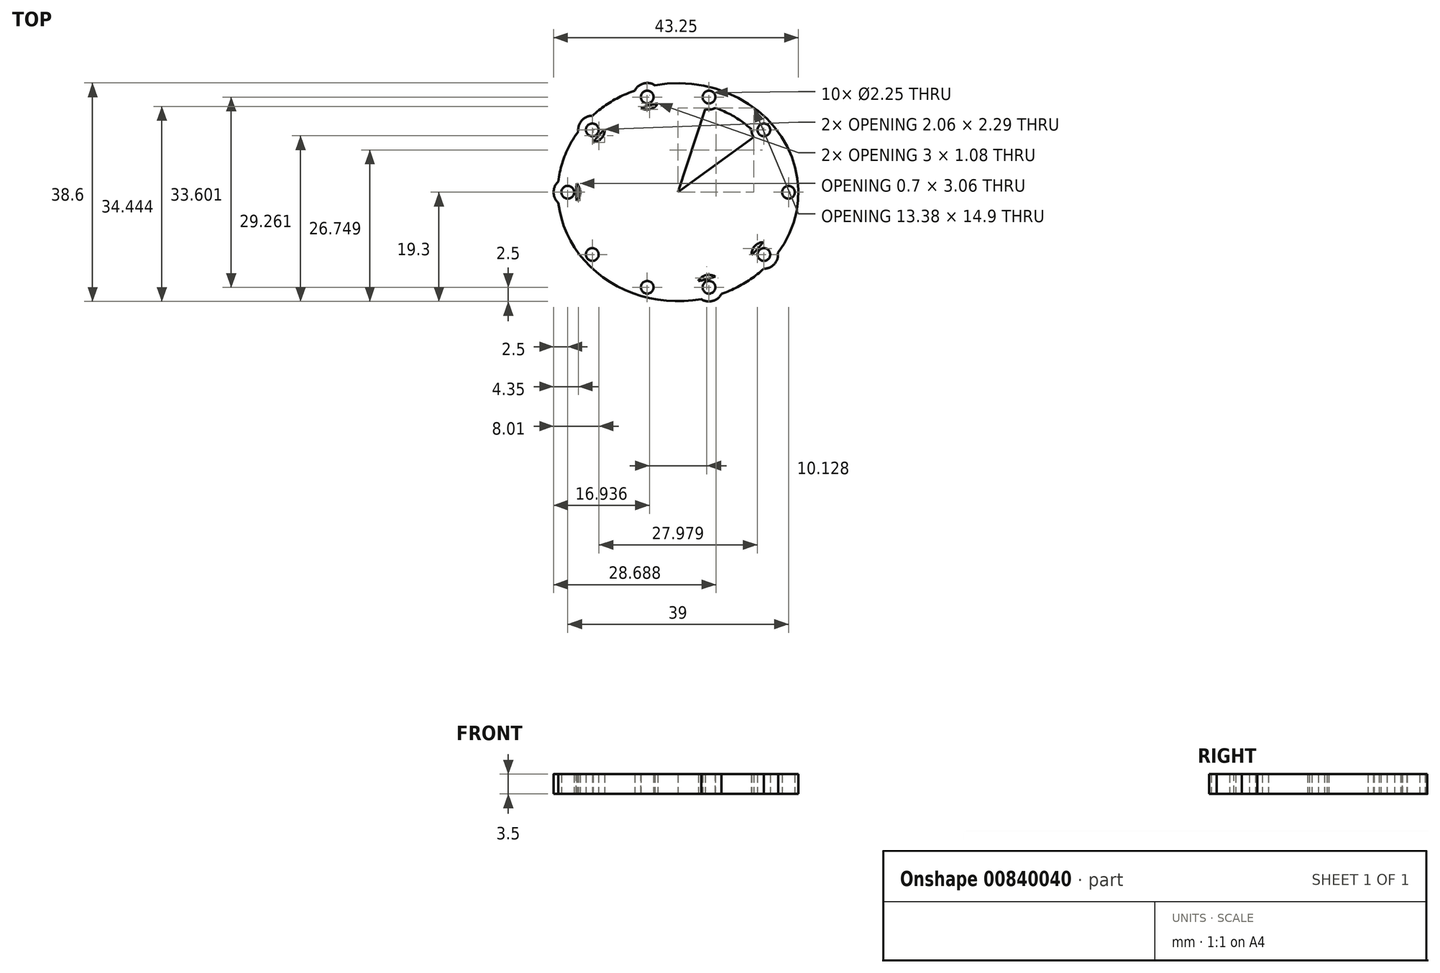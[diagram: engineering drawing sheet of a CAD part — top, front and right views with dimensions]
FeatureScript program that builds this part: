
annotation { "Feature Type Name" : "Feature", "Feature Type Description" : "" }
export const myFeature = defineFeature(function(context is Context, id is Id, definition is map)
    precondition{}
    {
        {
            var Q0;
            Q0=qCreatedBy(makeId("Top.planeOp"),FACE);
            var sketch = newSketch(context, id + "F0", { "sketchPlane" : qUnion([Q0])});
            skEllipse(sketch, "E0", {"center": v(0, 0) * mm, "majorRadius": 18 * mm, "minorRadius": 16 * mm, "majorAxis": v(1, 0)});
            skEllipse(sketch, "E1", {"center": v(0, 0) * mm, "majorRadius": 19.5 * mm, "minorRadius": 17.5 * mm, "majorAxis": v(1, 0)});
            skEllipse(sketch, "E2", {"center": v(0, 0) * mm, "majorRadius": 21.25 * mm, "minorRadius": 19.25 * mm, "majorAxis": v(1, 0)});
            skLineSegment(sketch, "E3", {"start": v(0, 0) * mm, "end": v(8.4, 25.87) * mm});
            skCircle(sketch, "E4", {"center": v(5.46, 16.8) * mm, "radius": 1.13 * mm});
            skLineSegment(sketch, "E5", {"start": v(0, 0) * mm, "end": v(30, 21.8) * mm});
            skCircle(sketch, "E6", {"center": v(15.16, 11.01) * mm, "radius": 1.13 * mm});
            skCircle(sketch, "E7", {"center": v(19.5, 0) * mm, "radius": 1.13 * mm});
            skCircle(sketch, "E8.MirrorC", {"center": v(15.16, -11.01) * mm, "radius": 1.13 * mm});
            skCircle(sketch, "E9.MirrorC", {"center": v(5.46, -16.8) * mm, "radius": 1.13 * mm});
            skCircle(sketch, "E10.MirrorC", {"center": v(-5.46, -16.8) * mm, "radius": 1.13 * mm});
            skCircle(sketch, "E11.MirrorC", {"center": v(-15.16, -11.01) * mm, "radius": 1.13 * mm});
            skCircle(sketch, "E12.MirrorC", {"center": v(-19.5, 0) * mm, "radius": 1.13 * mm});
            skCircle(sketch, "E13.MirrorC", {"center": v(-15.16, 11.01) * mm, "radius": 1.13 * mm});
            skCircle(sketch, "E14.MirrorC", {"center": v(-5.46, 16.8) * mm, "radius": 1.13 * mm});
            skArc(sketch, "E15", {"start": v(3.56, 15.68) * mm, "mid": v(4.9, 14.67) * mm, "end": v(6.56, 14.9) * mm});
            skArc(sketch, "E16", {"start": v(4.09, 18.9) * mm, "mid": v(6.1, 19.22) * mm, "end": v(7.68, 17.95) * mm});
            skArc(sketch, "E17", {"start": v(15.14, 13.51) * mm, "mid": v(17.01, 12.69) * mm, "end": v(17.64, 10.73) * mm});
            skArc(sketch, "E18", {"start": v(12.96, 11.1) * mm, "mid": v(13.52, 9.54) * mm, "end": v(15.02, 8.82) * mm});
            skArc(sketch, "E19", {"start": v(21.15, 1.88) * mm, "mid": v(22, 0) * mm, "end": v(21.15, -1.88) * mm});
            skArc(sketch, "E20", {"start": v(17.92, 1.53) * mm, "mid": v(17.3, 0) * mm, "end": v(17.92, -1.53) * mm});
            skArc(sketch, "E21.MirrorCS", {"start": v(12.96, -11.1) * mm, "mid": v(13.52, -9.54) * mm, "end": v(15.02, -8.82) * mm});
            skArc(sketch, "E22.MirrorCS", {"start": v(15.14, -13.51) * mm, "mid": v(17.01, -12.69) * mm, "end": v(17.64, -10.73) * mm});
            skArc(sketch, "E23.MirrorCS", {"start": v(3.56, -15.68) * mm, "mid": v(4.9, -14.67) * mm, "end": v(6.56, -14.9) * mm});
            skArc(sketch, "E24.MirrorCS", {"start": v(4.09, -18.9) * mm, "mid": v(6.1, -19.22) * mm, "end": v(7.68, -17.95) * mm});
            skArc(sketch, "E25.MirrorCS", {"start": v(-4.09, -18.9) * mm, "mid": v(-6.1, -19.22) * mm, "end": v(-7.68, -17.95) * mm});
            skArc(sketch, "E26.MirrorCS", {"start": v(-3.56, -15.68) * mm, "mid": v(-4.9, -14.67) * mm, "end": v(-6.56, -14.9) * mm});
            skArc(sketch, "E27.MirrorCS", {"start": v(-15.14, -13.51) * mm, "mid": v(-17.01, -12.69) * mm, "end": v(-17.64, -10.73) * mm});
            skArc(sketch, "E28.MirrorCS", {"start": v(-12.96, -11.1) * mm, "mid": v(-13.52, -9.54) * mm, "end": v(-15.02, -8.82) * mm});
            skArc(sketch, "E29.MirrorCS", {"start": v(-17.92, 1.53) * mm, "mid": v(-17.3, 0) * mm, "end": v(-17.92, -1.53) * mm});
            skArc(sketch, "E30.MirrorCS", {"start": v(-21.15, 1.88) * mm, "mid": v(-22, 0) * mm, "end": v(-21.15, -1.88) * mm});
            skArc(sketch, "E31.MirrorCS", {"start": v(-12.96, 11.1) * mm, "mid": v(-13.52, 9.54) * mm, "end": v(-15.02, 8.82) * mm});
            skArc(sketch, "E32.MirrorCS", {"start": v(-15.14, 13.51) * mm, "mid": v(-17.01, 12.69) * mm, "end": v(-17.64, 10.73) * mm});
            skArc(sketch, "E33.MirrorCS", {"start": v(-3.56, 15.68) * mm, "mid": v(-4.9, 14.67) * mm, "end": v(-6.56, 14.9) * mm});
            skArc(sketch, "E34.MirrorCS", {"start": v(-4.09, 18.9) * mm, "mid": v(-6.1, 19.22) * mm, "end": v(-7.68, 17.95) * mm});
            skSolve(sketch);
        }
        {
            var Q0;
            {var subQ9=sQuery(id+"F0.wireOp",EDGE,"E1");var subQ36=sQuery(id+"F0.wireOp",EDGE,"E6");var subQ37=makeQuery(id+"F0.imprint","INTERSECT",VERTEX,{"disambiguationData":[OD(0.0)],"derivedFrom":[subQ9,subQ36]});Q0=makeQuery(id+"F0.imprint","IMPRINT",FACE,{"disambiguationData":[TD([[makeQuery(id+"F0.imprint","IMPRINT",EDGE,{"disambiguationData":[TD([[subQ37,1.0]])],"derivedFrom":subQ9}),-1.0]])]});}
            var Q1;
            {var subQ6=sQuery(id+"F0.wireOp",EDGE,"E0");var subQ31=makeQuery(id+"F0.imprint","INTERSECT",VERTEX,{"disambiguationData":[OD(1.0)],"derivedFrom":[subQ6,sQuery(id+"F0.wireOp",EDGE,"E18")]});Q1=makeQuery(id+"F0.imprint","IMPRINT",FACE,{"disambiguationData":[TD([[makeQuery(id+"F0.imprint","IMPRINT",EDGE,{"disambiguationData":[TD([[subQ31,1.0]])],"derivedFrom":subQ6}),-1.0]])]});}
            var Q2;
            {var subQ5=sQuery(id+"F0.wireOp",EDGE,"E6");var subQ6=sQuery(id+"F0.wireOp",EDGE,"E1");var subQ7=makeQuery(id+"F0.imprint","INTERSECT",VERTEX,{"disambiguationData":[OD(1.0)],"derivedFrom":[subQ6,subQ5]});Q2=makeQuery(id+"F0.imprint","IMPRINT",FACE,{"disambiguationData":[TD([[makeQuery(id+"F0.imprint","IMPRINT",EDGE,{"disambiguationData":[TD([[subQ7,-1.0]])],"derivedFrom":subQ6}),-1.0]])]});}
            var Q3;
            {var subQ5=sQuery(id+"F0.wireOp",EDGE,"E0");var subQ7=makeQuery(id+"F0.imprint","INTERSECT",VERTEX,{"disambiguationData":[OD(0.0)],"derivedFrom":[subQ5,sQuery(id+"F0.wireOp",EDGE,"E18")]});Q3=makeQuery(id+"F0.imprint","IMPRINT",FACE,{"disambiguationData":[TD([[makeQuery(id+"F0.imprint","IMPRINT",EDGE,{"disambiguationData":[TD([[subQ7,1.0]])],"derivedFrom":subQ5}),-1.0]])]});}
            var Q4;
            {var subQ0=sQuery(id+"F0.wireOp",EDGE,"E16");var subQ1=sQuery(id+"F0.wireOp",EDGE,"E2");var subQ2=makeQuery(id+"F0.imprint","INTERSECT",VERTEX,{"disambiguationData":[OD(1.0)],"derivedFrom":[subQ1,subQ0]});Q4=makeQuery(id+"F0.imprint","IMPRINT",FACE,{"disambiguationData":[TD([[makeQuery(id+"F0.imprint","IMPRINT",EDGE,{"disambiguationData":[TD([[subQ2,-1.0]])],"derivedFrom":subQ1}),-1.0]])]});}
            var Q5;
            {var subQ0=sQuery(id+"F0.wireOp",EDGE,"E16");var subQ1=sQuery(id+"F0.wireOp",EDGE,"E2");var subQ2=makeQuery(id+"F0.imprint","INTERSECT",VERTEX,{"disambiguationData":[OD(0.0)],"derivedFrom":[subQ1,subQ0]});Q5=makeQuery(id+"F0.imprint","IMPRINT",FACE,{"disambiguationData":[TD([[makeQuery(id+"F0.imprint","IMPRINT",EDGE,{"disambiguationData":[TD([[subQ2,1.0]])],"derivedFrom":subQ1}),-1.0]])]});}
            var Q6;
            {var subQ0=sQuery(id+"F0.wireOp",EDGE,"E15");var subQ1=sQuery(id+"F0.wireOp",EDGE,"E0");var subQ2=makeQuery(id+"F0.imprint","INTERSECT",VERTEX,{"disambiguationData":[OD(0.0)],"derivedFrom":[subQ1,subQ0]});Q6=makeQuery(id+"F0.imprint","IMPRINT",FACE,{"disambiguationData":[TD([[makeQuery(id+"F0.imprint","IMPRINT",EDGE,{"disambiguationData":[TD([[subQ2,1.0]])],"derivedFrom":subQ1}),1.0]])]});}
            var Q7;
            {var subQ0=sQuery(id+"F0.wireOp",EDGE,"E15");var subQ1=sQuery(id+"F0.wireOp",EDGE,"E0");var subQ2=makeQuery(id+"F0.imprint","INTERSECT",VERTEX,{"disambiguationData":[OD(1.0)],"derivedFrom":[subQ1,subQ0]});Q7=makeQuery(id+"F0.imprint","IMPRINT",FACE,{"disambiguationData":[TD([[makeQuery(id+"F0.imprint","IMPRINT",EDGE,{"disambiguationData":[TD([[subQ2,-1.0]])],"derivedFrom":subQ1}),1.0]])]});}
            var Q8;
            {var subQ0=sQuery(id+"F0.wireOp",EDGE,"E17");var subQ1=sQuery(id+"F0.wireOp",EDGE,"E2");var subQ2=makeQuery(id+"F0.imprint","INTERSECT",VERTEX,{"disambiguationData":[OD(0.0)],"derivedFrom":[subQ1,subQ0]});Q8=makeQuery(id+"F0.imprint","IMPRINT",FACE,{"disambiguationData":[TD([[makeQuery(id+"F0.imprint","IMPRINT",EDGE,{"disambiguationData":[TD([[subQ2,1.0]])],"derivedFrom":subQ1}),-1.0]])]});}
            var Q9;
            {var subQ0=sQuery(id+"F0.wireOp",EDGE,"E17");var subQ1=sQuery(id+"F0.wireOp",EDGE,"E2");var subQ2=makeQuery(id+"F0.imprint","INTERSECT",VERTEX,{"disambiguationData":[OD(1.0)],"derivedFrom":[subQ1,subQ0]});Q9=makeQuery(id+"F0.imprint","IMPRINT",FACE,{"disambiguationData":[TD([[makeQuery(id+"F0.imprint","IMPRINT",EDGE,{"disambiguationData":[TD([[subQ2,-1.0]])],"derivedFrom":subQ1}),-1.0]])]});}
            var Q10;
            {var subQ0=sQuery(id+"F0.wireOp",EDGE,"E18");var subQ1=sQuery(id+"F0.wireOp",EDGE,"E0");var subQ2=makeQuery(id+"F0.imprint","INTERSECT",VERTEX,{"disambiguationData":[OD(1.0)],"derivedFrom":[subQ1,subQ0]});Q10=makeQuery(id+"F0.imprint","IMPRINT",FACE,{"disambiguationData":[TD([[makeQuery(id+"F0.imprint","IMPRINT",EDGE,{"disambiguationData":[TD([[subQ2,-1.0]])],"derivedFrom":subQ1}),1.0]])]});}
            var Q11;
            {var subQ0=sQuery(id+"F0.wireOp",EDGE,"E18");var subQ1=sQuery(id+"F0.wireOp",EDGE,"E0");var subQ2=makeQuery(id+"F0.imprint","INTERSECT",VERTEX,{"disambiguationData":[OD(0.0)],"derivedFrom":[subQ1,subQ0]});Q11=makeQuery(id+"F0.imprint","IMPRINT",FACE,{"disambiguationData":[TD([[makeQuery(id+"F0.imprint","IMPRINT",EDGE,{"disambiguationData":[TD([[subQ2,1.0]])],"derivedFrom":subQ1}),1.0]])]});}
            var Q12;
            {var subQ0=sQuery(id+"F0.wireOp",EDGE,"E19");Q12=makeQuery(id+"F0.imprint","IMPRINT",FACE,{"disambiguationData":[TD([[makeQuery(id+"F0.imprint","IMPRINT",EDGE,{"derivedFrom":subQ0}),-1.0]])]});}
            var Q13;
            {var subQ0=sQuery(id+"F0.wireOp",EDGE,"E20");Q13=makeQuery(id+"F0.imprint","IMPRINT",FACE,{"disambiguationData":[TD([[makeQuery(id+"F0.imprint","IMPRINT",EDGE,{"derivedFrom":subQ0}),1.0]])]});}
            var Q14;
            {var subQ0=sQuery(id+"F0.wireOp",EDGE,"E22.MirrorCS");Q14=makeQuery(id+"F0.imprint","IMPRINT",FACE,{"disambiguationData":[TD([[makeQuery(id+"F0.imprint","IMPRINT",EDGE,{"derivedFrom":subQ0}),1.0]])]});}
            var Q15;
            {var subQ0=sQuery(id+"F0.wireOp",EDGE,"E21.MirrorCS");Q15=makeQuery(id+"F0.imprint","IMPRINT",FACE,{"disambiguationData":[TD([[makeQuery(id+"F0.imprint","IMPRINT",EDGE,{"derivedFrom":subQ0}),-1.0]])]});}
            var Q16;
            {var subQ0=sQuery(id+"F0.wireOp",EDGE,"E34.MirrorCS");Q16=makeQuery(id+"F0.imprint","IMPRINT",FACE,{"disambiguationData":[TD([[makeQuery(id+"F0.imprint","IMPRINT",EDGE,{"derivedFrom":subQ0}),1.0]])]});}
            var Q17;
            {var subQ0=sQuery(id+"F0.wireOp",EDGE,"E33.MirrorCS");Q17=makeQuery(id+"F0.imprint","IMPRINT",FACE,{"disambiguationData":[TD([[makeQuery(id+"F0.imprint","IMPRINT",EDGE,{"derivedFrom":subQ0}),-1.0]])]});}
            var Q18;
            {var subQ0=sQuery(id+"F0.wireOp",EDGE,"E32.MirrorCS");Q18=makeQuery(id+"F0.imprint","IMPRINT",FACE,{"disambiguationData":[TD([[makeQuery(id+"F0.imprint","IMPRINT",EDGE,{"derivedFrom":subQ0}),1.0]])]});}
            var Q19;
            {var subQ0=sQuery(id+"F0.wireOp",EDGE,"E31.MirrorCS");Q19=makeQuery(id+"F0.imprint","IMPRINT",FACE,{"disambiguationData":[TD([[makeQuery(id+"F0.imprint","IMPRINT",EDGE,{"derivedFrom":subQ0}),-1.0]])]});}
            var Q20;
            {var subQ0=sQuery(id+"F0.wireOp",EDGE,"E29.MirrorCS");Q20=makeQuery(id+"F0.imprint","IMPRINT",FACE,{"disambiguationData":[TD([[makeQuery(id+"F0.imprint","IMPRINT",EDGE,{"derivedFrom":subQ0}),-1.0]])]});}
            var Q21;
            {var subQ0=sQuery(id+"F0.wireOp",EDGE,"E30.MirrorCS");Q21=makeQuery(id+"F0.imprint","IMPRINT",FACE,{"disambiguationData":[TD([[makeQuery(id+"F0.imprint","IMPRINT",EDGE,{"derivedFrom":subQ0}),1.0]])]});}
            var Q22;
            {var subQ0=sQuery(id+"F0.wireOp",EDGE,"E27.MirrorCS");Q22=makeQuery(id+"F0.imprint","IMPRINT",FACE,{"disambiguationData":[TD([[makeQuery(id+"F0.imprint","IMPRINT",EDGE,{"derivedFrom":subQ0}),-1.0]])]});}
            var Q23;
            {var subQ0=sQuery(id+"F0.wireOp",EDGE,"E28.MirrorCS");Q23=makeQuery(id+"F0.imprint","IMPRINT",FACE,{"disambiguationData":[TD([[makeQuery(id+"F0.imprint","IMPRINT",EDGE,{"derivedFrom":subQ0}),1.0]])]});}
            var Q24;
            {var subQ0=sQuery(id+"F0.wireOp",EDGE,"E26.MirrorCS");Q24=makeQuery(id+"F0.imprint","IMPRINT",FACE,{"disambiguationData":[TD([[makeQuery(id+"F0.imprint","IMPRINT",EDGE,{"derivedFrom":subQ0}),1.0]])]});}
            var Q25;
            {var subQ0=sQuery(id+"F0.wireOp",EDGE,"E25.MirrorCS");Q25=makeQuery(id+"F0.imprint","IMPRINT",FACE,{"disambiguationData":[TD([[makeQuery(id+"F0.imprint","IMPRINT",EDGE,{"derivedFrom":subQ0}),-1.0]])]});}
            var Q26;
            {var subQ0=sQuery(id+"F0.wireOp",EDGE,"E23.MirrorCS");Q26=makeQuery(id+"F0.imprint","IMPRINT",FACE,{"disambiguationData":[TD([[makeQuery(id+"F0.imprint","IMPRINT",EDGE,{"derivedFrom":subQ0}),-1.0]])]});}
            var Q27;
            {var subQ0=sQuery(id+"F0.wireOp",EDGE,"E24.MirrorCS");Q27=makeQuery(id+"F0.imprint","IMPRINT",FACE,{"disambiguationData":[TD([[makeQuery(id+"F0.imprint","IMPRINT",EDGE,{"derivedFrom":subQ0}),1.0]])]});}
            extrude(context, id + "F1", {"entities" : qUnion([Q0, Q1, Q2, Q3, Q4, Q5, Q6, Q7, Q8, Q9, Q10, Q11, Q12, Q13, Q14, Q15, Q16, Q17, Q18, Q19, Q20, Q21, Q22, Q23, Q24, Q25, Q26, Q27]), "depth" : 3.5 * mm, "offsetDistance" : 25 * mm});
        }
    });
